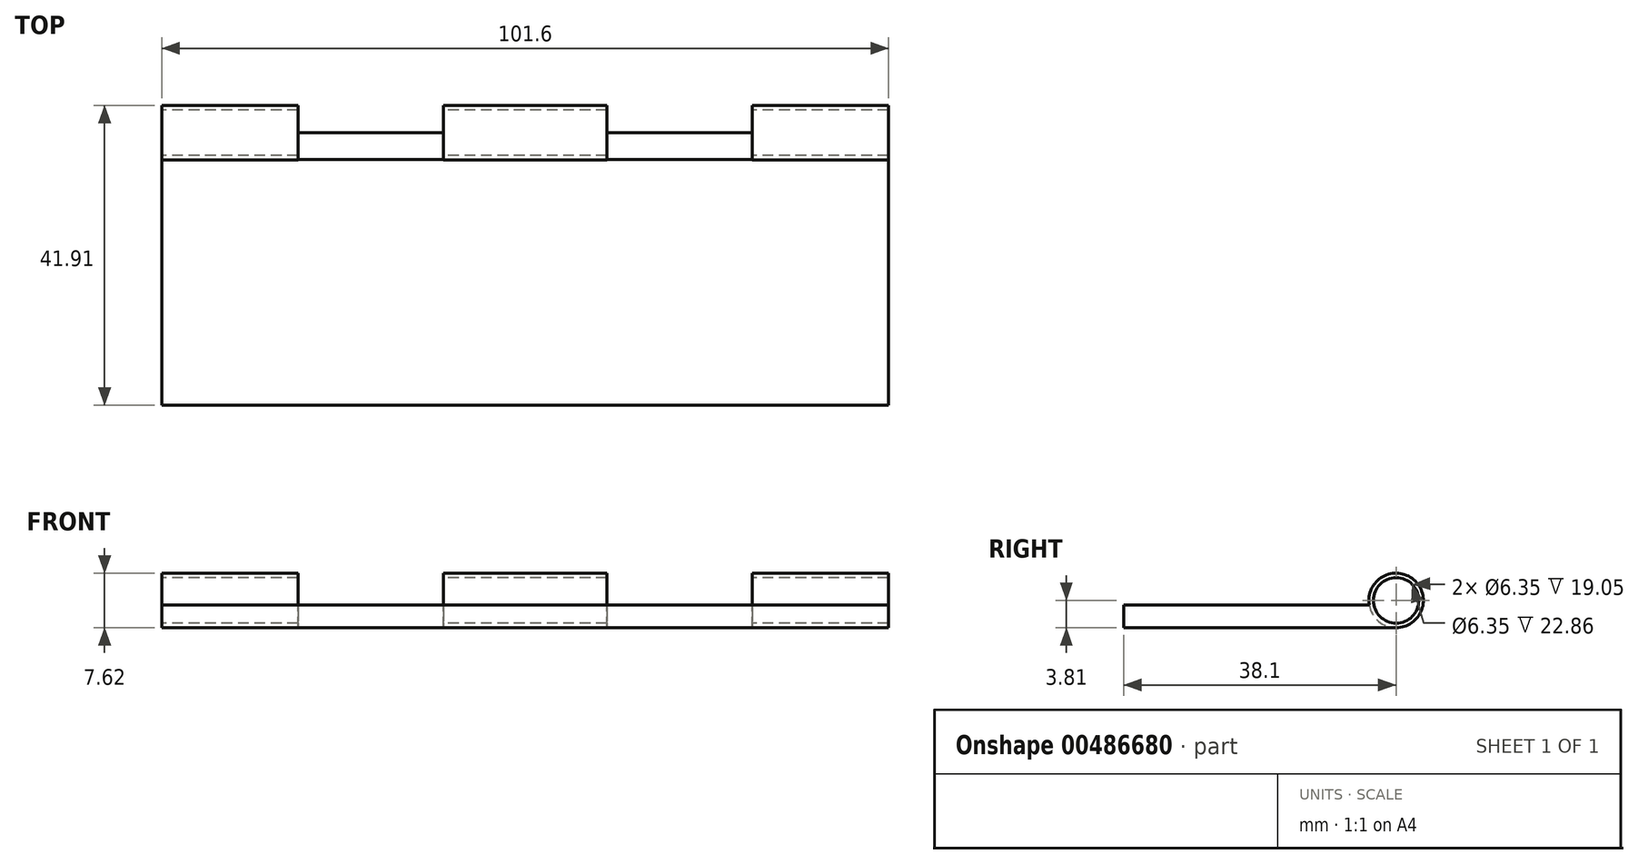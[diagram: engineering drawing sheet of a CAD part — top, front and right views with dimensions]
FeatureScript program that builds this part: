
annotation { "Feature Type Name" : "Feature", "Feature Type Description" : "" }
export const myFeature = defineFeature(function(context is Context, id is Id, definition is map)
    precondition{}
    {
        {
            var Q0;
            Q0=qCreatedBy(makeId("Top.planeOp"),FACE);
            var sketch = newSketch(context, id + "F0", { "sketchPlane" : qUnion([Q0])});
            skLineSegment(sketch, "E0.bottom", {"start": v(0, 0) * mm, "end": v(-101.6, 0) * mm});
            skLineSegment(sketch, "E0.top", {"start": v(0, -38.1) * mm, "end": v(-101.6, -38.1) * mm});
            skLineSegment(sketch, "E0.left", {"start": v(0, 0) * mm, "end": v(0, -38.1) * mm});
            skLineSegment(sketch, "E0.right", {"start": v(-101.6, 0) * mm, "end": v(-101.6, -38.1) * mm});
            skSolve(sketch);
        }
        {
            var Q0;
            Q0=qSketchRegion(id+"F0",true);
            extrude(context, id + "F1", {"entities" : qUnion([Q0]), "depth" : 3.17 * mm});
        }
        {
            var Q0;
            Q0=makeQuery(id+"F1.opExtrude","SWEPT_FACE",FACE,{"disambiguationData":[OSD([sQuery(id+"F0.wireOp",EDGE,"E0.right")])]});
            var sketch = newSketch(context, id + "F2", { "sketchPlane" : qUnion([Q0])});
            skCircle(sketch, "E1", {"center": v(0, 3.81) * mm, "radius": 3.81 * mm});
            skCircle(sketch, "E2", {"center": v(0, 3.81) * mm, "radius": 3.18 * mm});
            skSolve(sketch);
        }
        {
            var Q0;
            {var subQ0=sQuery(id+"F2.wireOp",EDGE,"E1");var subQ1=sQuery(id+"F0.wireOp",EDGE,"E0.right");var subQ4=makeQuery(id+"F1.opExtrude","CAP_EDGE",EDGE,{"disambiguationData":[OSD([subQ1])],"isStart":false});var subQ5=makeQuery(id+"F2.imprint","INTERSECT",VERTEX,{"derivedFrom":[subQ4,subQ0]});Q0=makeQuery(id+"F2.imprint","IMPRINT",FACE,{"disambiguationData":[TD([[makeQuery(id+"F2.imprint","IMPRINT",EDGE,{"disambiguationData":[TD([[subQ5,1.0]])],"derivedFrom":subQ4}),1.0]])]});}
            var Q1;
            {var subQ0=sQuery(id+"F2.wireOp",EDGE,"E1");var subQ1=sQuery(id+"F0.wireOp",EDGE,"E0.right");var subQ4=makeQuery(id+"F1.opExtrude","CAP_EDGE",EDGE,{"disambiguationData":[OSD([subQ1])],"isStart":false});var subQ5=makeQuery(id+"F2.imprint","INTERSECT",VERTEX,{"derivedFrom":[subQ4,subQ0]});Q1=makeQuery(id+"F2.imprint","IMPRINT",FACE,{"disambiguationData":[TD([[makeQuery(id+"F2.imprint","IMPRINT",EDGE,{"disambiguationData":[TD([[subQ5,1.0]])],"derivedFrom":subQ4}),-1.0]])]});}
            var Q2;
            {var subQ0=sQuery(id+"F2.wireOp",EDGE,"E2");var subQ1=sQuery(id+"F0.wireOp",EDGE,"E0.right");var subQ4=makeQuery(id+"F1.opExtrude","CAP_EDGE",EDGE,{"disambiguationData":[OSD([subQ1])],"isStart":false});var subQ5=makeQuery(id+"F2.imprint","INTERSECT",VERTEX,{"derivedFrom":[subQ4,subQ0]});Q2=makeQuery(id+"F2.imprint","IMPRINT",FACE,{"disambiguationData":[TD([[makeQuery(id+"F2.imprint","IMPRINT",EDGE,{"disambiguationData":[TD([[subQ5,1.0]])],"derivedFrom":subQ0}),1.0]])]});}
            var Q3;
            Q3=makeQuery(id+"F1.opExtrude","SWEPT_FACE",FACE,{"disambiguationData":[OSD([sQuery(id+"F0.wireOp",EDGE,"E0.left")])]});
            extrude(context, id + "F3", {"entities" : qUnion([Q0, Q1, Q2]), "operationType" : NewBodyOperationType.REMOVE, "oppositeDirection" : true, "endBoundEntityFace" : qUnion([Q3]), "depth" : 254 * mm});
        }
        {
            var Q0;
            Q0=qSketchRegion(id+"F2",true);
            var Q1;
            Q1=makeQuery(id+"F1.opExtrude","SWEPT_FACE",FACE,{"disambiguationData":[OSD([sQuery(id+"F0.wireOp",EDGE,"E0.left")])]});
            extrude(context, id + "F4", {"entities" : qUnion([Q0]), "operationType" : NewBodyOperationType.ADD, "endBound" : BoundingType.UP_TO_SURFACE, "oppositeDirection" : true, "endBoundEntityFace" : qUnion([Q1]), "depth" : 25.4 * mm});
        }
        {
            var Q0;
            Q0=qSketchRegion(id+"F2",true);
            extrude(context, id + "F5", {"entities" : qUnion([Q0]), "operationType" : NewBodyOperationType.REMOVE, "oppositeDirection" : true, "depth" : 39.37 * mm, "hasSecondDirection" : true, "secondDirectionOppositeDirection" : true, "secondDirectionDepth" : 19.05 * mm});
        }
        {
            var Q0;
            Q0=qSketchRegion(id+"F2",true);
            extrude(context, id + "F6", {"entities" : qUnion([Q0]), "operationType" : NewBodyOperationType.REMOVE, "oppositeDirection" : true, "depth" : 82.55 * mm, "hasSecondDirection" : true, "secondDirectionOppositeDirection" : true, "secondDirectionDepth" : 62.23 * mm});
        }
    });
